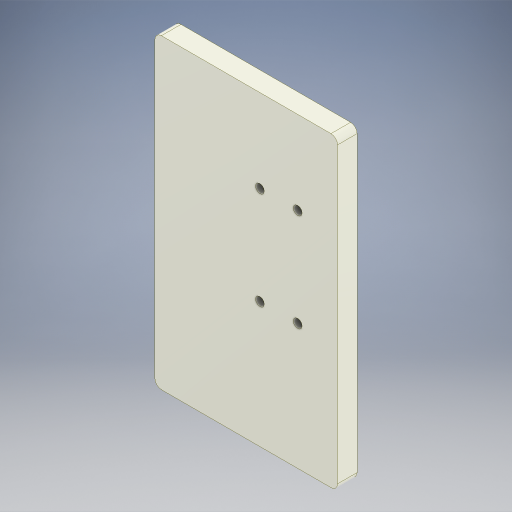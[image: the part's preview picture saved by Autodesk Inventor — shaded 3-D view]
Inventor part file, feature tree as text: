
AUTODESK INVENTOR PART (.ipt)
format: ipt  version: 2024 (Build 280153000, 153)  size: 339,456 bytes
history: native  units: in
note: dims shown in document units (in); Inventor stores cm internally (conversion verified against a paired STEP export)
features: reference x6, extrude x5, sketch x5, other x4, fillet x1
ambient origin geometry x8: Origin, YZ Plane, XZ Plane, XY Plane, X Axis, Y Axis, Z Axis, Center Point
bodies: Body1 (feature_tree)
feature tree (21):
  other  "솔리드1"
  extrude  "돌출1"  Depth=2.2047in
  fillet  "모깎기1"  Radius=3.7008in
  extrude  "돌출2"  Depth=0.1063in
  extrude  "돌출3"  Depth=0.1063in
  extrude  "돌출4"  Depth=0.1063in
  extrude  "돌출5"  Depth=0.1063in
  sketch  "스케치1"
  reference  "참조1"
  reference  "참조2"
  reference  "참조3"
  reference  "참조4"
  reference  "참조5"
  reference  "참조6"
  sketch  "스케치3"
  sketch  "스케치4"
  sketch  "스케치5"
  sketch  "스케치6"
  other  "조립품13"
  other  "foot_right_64:2"
  other  "foot_right_64:1"
